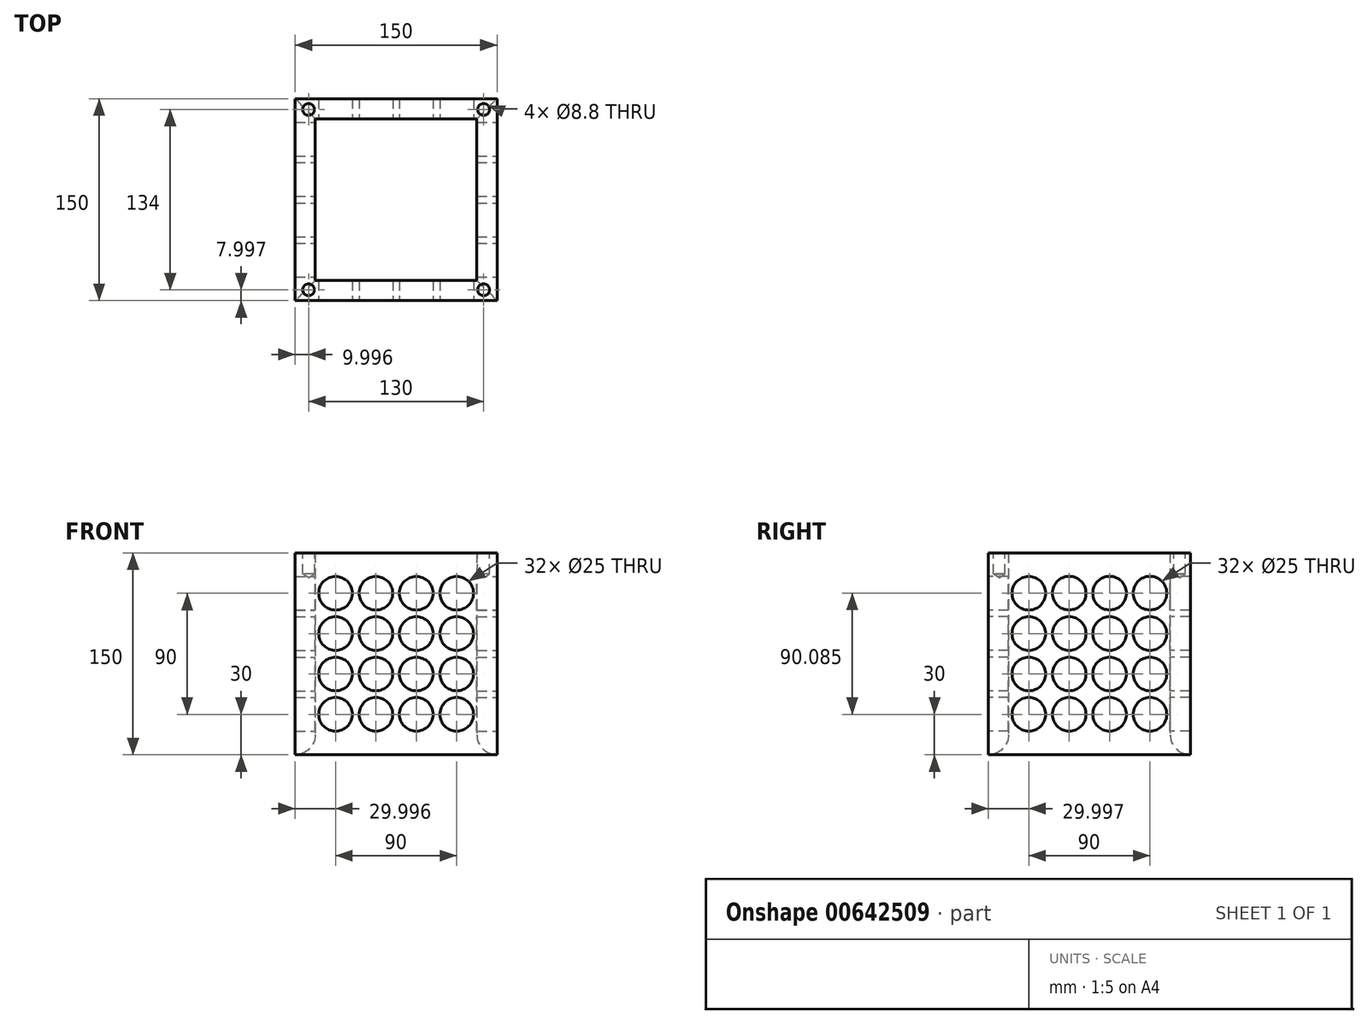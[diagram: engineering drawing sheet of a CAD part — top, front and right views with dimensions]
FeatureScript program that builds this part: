
annotation { "Feature Type Name" : "Feature", "Feature Type Description" : "" }
export const myFeature = defineFeature(function(context is Context, id is Id, definition is map)
    precondition{}
    {
        {
            var Q0;
            Q0=qCreatedBy(makeId("Top.planeOp"),FACE);
            var sketch = newSketch(context, id + "F0", { "sketchPlane" : qUnion([Q0])});
            skLineSegment(sketch, "E0.bottom", {"start": v(-58.65, 45.53) * mm, "end": v(-208.65, 45.53) * mm});
            skLineSegment(sketch, "E0.top", {"start": v(-58.65, -104.47) * mm, "end": v(-208.65, -104.47) * mm});
            skLineSegment(sketch, "E0.left", {"start": v(-58.65, 45.53) * mm, "end": v(-58.65, -104.47) * mm});
            skLineSegment(sketch, "E0.right", {"start": v(-208.65, 45.53) * mm, "end": v(-208.65, -104.47) * mm});
            skSolve(sketch);
        }
        {
            var Q0;
            Q0=makeQuery(id+"F0.imprint","IMPRINT",FACE,{"disambiguationData":[TD([[makeQuery(id+"F0.imprint","IMPRINT",EDGE,{"derivedFrom":sQuery(id+"F0.wireOp",EDGE,"E0.bottom")}),1.0]])]});
            extrude(context, id + "F1", {"entities" : qUnion([Q0]), "depth" : 150 * mm, "offsetDistance" : 25 * mm});
        }
        {
            var Q0;
            Q0=makeQuery(id+"F1.opExtrude","CAP_FACE",FACE,{"disambiguationData":[OSD([sQuery(id+"F0.wireOp",EDGE,"E0.bottom"),sQuery(id+"F0.wireOp",EDGE,"E0.top"),sQuery(id+"F0.wireOp",EDGE,"E0.left"),sQuery(id+"F0.wireOp",EDGE,"E0.right")])],"isStart":true});
            var Q1;
            Q1=makeQuery(id+"F1.opExtrude","CAP_FACE",FACE,{"disambiguationData":[OSD([sQuery(id+"F0.wireOp",EDGE,"E0.bottom"),sQuery(id+"F0.wireOp",EDGE,"E0.top"),sQuery(id+"F0.wireOp",EDGE,"E0.left"),sQuery(id+"F0.wireOp",EDGE,"E0.right")])],"isStart":false});
            shell(context, id + "F2", {"entities" : qUnion([Q0, Q1]), "thickness" : 15 * mm});
        }
        {
            var Q0;
            Q0=makeQuery(id+"F1.opExtrude","SWEPT_FACE",FACE,{"disambiguationData":[OSD([sQuery(id+"F0.wireOp",EDGE,"E0.top")])]});
            var sketch = newSketch(context, id + "F3", { "sketchPlane" : qUnion([Q0])});
            skPoint(sketch, "E1", {"position": v(-178.65, 120) * mm});
            skPoint(sketch, "E2", {"position": v(-178.65, 90) * mm});
            skPoint(sketch, "E3", {"position": v(-178.65, 60) * mm});
            skPoint(sketch, "E4", {"position": v(-178.65, 30) * mm});
            skPoint(sketch, "E5", {"position": v(-148.65, 120) * mm});
            skPoint(sketch, "E6", {"position": v(-118.65, 120) * mm});
            skPoint(sketch, "E7", {"position": v(-88.65, 120) * mm});
            skPoint(sketch, "E8", {"position": v(-148.65, 90) * mm});
            skPoint(sketch, "E9", {"position": v(-148.65, 60) * mm});
            skPoint(sketch, "E10", {"position": v(-148.65, 30) * mm});
            skPoint(sketch, "E11", {"position": v(-118.65, 90) * mm});
            skPoint(sketch, "E12", {"position": v(-118.65, 60) * mm});
            skPoint(sketch, "E13", {"position": v(-118.65, 30) * mm});
            skPoint(sketch, "E14", {"position": v(-88.65, 90) * mm});
            skPoint(sketch, "E15", {"position": v(-88.65, 60) * mm});
            skPoint(sketch, "E16", {"position": v(-88.65, 30) * mm});
            skSolve(sketch);
        }
        {
            var Q0;
            Q0=sQuery(id+"F3.wireOp",VERTEX,"E1");
            var Q1;
            Q1=sQuery(id+"F3.wireOp",VERTEX,"E5");
            var Q2;
            Q2=sQuery(id+"F3.wireOp",VERTEX,"E6");
            var Q3;
            Q3=sQuery(id+"F3.wireOp",VERTEX,"E7");
            var Q4;
            Q4=sQuery(id+"F3.wireOp",VERTEX,"E2");
            var Q5;
            Q5=sQuery(id+"F3.wireOp",VERTEX,"E8");
            var Q6;
            Q6=sQuery(id+"F3.wireOp",VERTEX,"E11");
            var Q7;
            Q7=sQuery(id+"F3.wireOp",VERTEX,"E14");
            var Q8;
            Q8=sQuery(id+"F3.wireOp",VERTEX,"E15");
            var Q9;
            Q9=sQuery(id+"F3.wireOp",VERTEX,"E12");
            var Q10;
            Q10=sQuery(id+"F3.wireOp",VERTEX,"E9");
            var Q11;
            Q11=sQuery(id+"F3.wireOp",VERTEX,"E3");
            var Q12;
            Q12=sQuery(id+"F3.wireOp",VERTEX,"E4");
            var Q13;
            Q13=sQuery(id+"F3.wireOp",VERTEX,"E10");
            var Q14;
            Q14=sQuery(id+"F3.wireOp",VERTEX,"E13");
            var Q15;
            Q15=sQuery(id+"F3.wireOp",VERTEX,"E16");
            var Q16;
            Q16=makeQuery(id+"F1.opExtrude","SWEPT_BODY",BODY,{"disambiguationData":[OSD([sQuery(id+"F0.wireOp",EDGE,"E0.bottom"),sQuery(id+"F0.wireOp",EDGE,"E0.top"),sQuery(id+"F0.wireOp",EDGE,"E0.left"),sQuery(id+"F0.wireOp",EDGE,"E0.right")])]});
            hole(context, id + "F4", {"style" : HoleStyle.SIMPLE, "endStyle" : HoleEndStyle.THROUGH, "holeDiameter" : 25 * mm, "majorDiameter" : 5 * mm, "isTappedThrough" : true, "tappedDepth" : 12 * mm, "tapClearance" : 3, "locations" : qUnion([Q0, Q1, Q2, Q3, Q4, Q5, Q6, Q7, Q8, Q9, Q10, Q11, Q12, Q13, Q14, Q15]), "scope" : qUnion([Q16])});
        }
        {
            var Q0;
            Q0=makeQuery(id+"F1.opExtrude","SWEPT_FACE",FACE,{"disambiguationData":[OSD([sQuery(id+"F0.wireOp",EDGE,"E0.left")])]});
            var sketch = newSketch(context, id + "F5", { "sketchPlane" : qUnion([Q0])});
            skPoint(sketch, "E17", {"position": v(-74.47, 205.73) * mm});
            skPoint(sketch, "E18", {"position": v(-38.58, 205.73) * mm});
            skPoint(sketch, "E19", {"position": v(8.94, 205.73) * mm});
            skPoint(sketch, "E20", {"position": v(0, 205.73) * mm});
            skPoint(sketch, "E21", {"position": v(-74.47, 176.17) * mm});
            skPoint(sketch, "E22", {"position": v(-74.47, 120) * mm});
            skPoint(sketch, "E23", {"position": v(-74.47, 90) * mm});
            skPoint(sketch, "E24", {"position": v(-74.47, 60) * mm});
            skPoint(sketch, "E25", {"position": v(-74.47, 30) * mm});
            skPoint(sketch, "E26", {"position": v(-44.47, 120.08) * mm});
            skPoint(sketch, "E27", {"position": v(-14.47, 120.08) * mm});
            skPoint(sketch, "E28", {"position": v(15.53, 120.08) * mm});
            skPoint(sketch, "E29", {"position": v(-44.47, 90) * mm});
            skPoint(sketch, "E30", {"position": v(-44.47, 60) * mm});
            skPoint(sketch, "E31", {"position": v(-44.47, 30) * mm});
            skPoint(sketch, "E32", {"position": v(-14.47, 90) * mm});
            skPoint(sketch, "E33", {"position": v(15.53, 90) * mm});
            skPoint(sketch, "E34", {"position": v(15.53, 60) * mm});
            skPoint(sketch, "E35", {"position": v(-14.47, 60) * mm});
            skPoint(sketch, "E36", {"position": v(-14.47, 30) * mm});
            skPoint(sketch, "E37", {"position": v(15.53, 30) * mm});
            skSolve(sketch);
        }
        {
            var Q0;
            Q0=sQuery(id+"F5.wireOp",VERTEX,"E22");
            var Q1;
            Q1=sQuery(id+"F5.wireOp",VERTEX,"E26");
            var Q2;
            Q2=sQuery(id+"F5.wireOp",VERTEX,"E27");
            var Q3;
            Q3=sQuery(id+"F5.wireOp",VERTEX,"E28");
            var Q4;
            Q4=sQuery(id+"F5.wireOp",VERTEX,"E23");
            var Q5;
            Q5=sQuery(id+"F5.wireOp",VERTEX,"E29");
            var Q6;
            Q6=sQuery(id+"F5.wireOp",VERTEX,"E32");
            var Q7;
            Q7=sQuery(id+"F5.wireOp",VERTEX,"E33");
            var Q8;
            Q8=sQuery(id+"F5.wireOp",VERTEX,"E34");
            var Q9;
            Q9=sQuery(id+"F5.wireOp",VERTEX,"E35");
            var Q10;
            Q10=sQuery(id+"F5.wireOp",VERTEX,"E30");
            var Q11;
            Q11=sQuery(id+"F5.wireOp",VERTEX,"E24");
            var Q12;
            Q12=sQuery(id+"F5.wireOp",VERTEX,"E25");
            var Q13;
            Q13=sQuery(id+"F5.wireOp",VERTEX,"E31");
            var Q14;
            Q14=sQuery(id+"F5.wireOp",VERTEX,"E36");
            var Q15;
            Q15=sQuery(id+"F5.wireOp",VERTEX,"E37");
            var Q16;
            Q16=makeQuery(id+"F1.opExtrude","SWEPT_BODY",BODY,{"disambiguationData":[OSD([sQuery(id+"F0.wireOp",EDGE,"E0.bottom"),sQuery(id+"F0.wireOp",EDGE,"E0.top"),sQuery(id+"F0.wireOp",EDGE,"E0.left"),sQuery(id+"F0.wireOp",EDGE,"E0.right")])]});
            hole(context, id + "F6", {"style" : HoleStyle.SIMPLE, "endStyle" : HoleEndStyle.THROUGH, "holeDiameter" : 25 * mm, "majorDiameter" : 5 * mm, "isTappedThrough" : true, "tappedDepth" : 12 * mm, "tapClearance" : 3, "locations" : qUnion([Q0, Q1, Q2, Q3, Q4, Q5, Q6, Q7, Q8, Q9, Q10, Q11, Q12, Q13, Q14, Q15]), "scope" : qUnion([Q16])});
        }
        {
            var Q0;
            {var subQ0=sQuery(id+"F0.wireOp",EDGE,"E0.top");Q0=makeQuery(id+"F2.opShell","OFFSET_EDGE",EDGE,{"disambiguationData":[OSD([subQ0]),TDD([makeQuery(id+"F1.opExtrude","CAP_EDGE",EDGE,{"disambiguationData":[OSD([subQ0])],"isStart":true})])]});}
            var Q1;
            {var subQ0=sQuery(id+"F0.wireOp",EDGE,"E0.left");Q1=makeQuery(id+"F2.opShell","OFFSET_EDGE",EDGE,{"disambiguationData":[OSD([subQ0]),TDD([makeQuery(id+"F1.opExtrude","CAP_EDGE",EDGE,{"disambiguationData":[OSD([subQ0])],"isStart":true})])]});}
            var Q2;
            {var subQ0=sQuery(id+"F0.wireOp",EDGE,"E0.bottom");Q2=makeQuery(id+"F2.opShell","OFFSET_EDGE",EDGE,{"disambiguationData":[OSD([subQ0]),TDD([makeQuery(id+"F1.opExtrude","CAP_EDGE",EDGE,{"disambiguationData":[OSD([subQ0])],"isStart":true})])]});}
            var Q3;
            {var subQ0=sQuery(id+"F0.wireOp",EDGE,"E0.right");Q3=makeQuery(id+"F2.opShell","OFFSET_EDGE",EDGE,{"disambiguationData":[OSD([subQ0]),TDD([makeQuery(id+"F1.opExtrude","CAP_EDGE",EDGE,{"disambiguationData":[OSD([subQ0])],"isStart":true})])]});}
            fillet(context, id + "F7", {"entities" : qUnion([Q0, Q1, Q2, Q3]), "radius" : 15 * mm, "tangentPropagation" : true, "allowEdgeOverflow" : false});
        }
        {
            var Q0;
            Q0=makeQuery(id+"F1.opExtrude","CAP_FACE",FACE,{"disambiguationData":[OSD([sQuery(id+"F0.wireOp",EDGE,"E0.bottom"),sQuery(id+"F0.wireOp",EDGE,"E0.top"),sQuery(id+"F0.wireOp",EDGE,"E0.left"),sQuery(id+"F0.wireOp",EDGE,"E0.right")])],"isStart":false});
            var sketch = newSketch(context, id + "F8", { "sketchPlane" : qUnion([Q0])});
            skPoint(sketch, "E38", {"position": v(-198.65, 37.53) * mm});
            skPoint(sketch, "E39", {"position": v(-68.65, -96.47) * mm});
            skPoint(sketch, "E40", {"position": v(-68.65, 37.53) * mm});
            skPoint(sketch, "E41", {"position": v(-198.65, -96.47) * mm});
            skSolve(sketch);
        }
        {
            var Q0;
            {var subQ6=sQuery(id+"F0.wireOp",EDGE,"E0.bottom");var subQ7=makeQuery(id+"F1.opExtrude","CAP_EDGE",EDGE,{"disambiguationData":[OSD([subQ6])],"isStart":false});Q0=makeQuery(id+"F8.imprint","IMPRINT",FACE,{"disambiguationData":[TD([[makeQuery(id+"F8.imprint","IMPRINT",EDGE,{"derivedFrom":subQ7}),1.0]])]});}
            var sketch = newSketch(context, id + "F9", { "sketchPlane" : qUnion([Q0])});
            skSolve(sketch);
        }
        {
            var Q0;
            Q0=sQuery(id+"F8.wireOp",VERTEX,"E38");
            var Q1;
            Q1=sQuery(id+"F8.wireOp",VERTEX,"E40");
            var Q2;
            Q2=sQuery(id+"F8.wireOp",VERTEX,"E39");
            var Q3;
            Q3=sQuery(id+"F8.wireOp",VERTEX,"E41");
            var Q4;
            Q4=makeQuery(id+"F1.opExtrude","SWEPT_BODY",BODY,{"disambiguationData":[OSD([sQuery(id+"F0.wireOp",EDGE,"E0.bottom"),sQuery(id+"F0.wireOp",EDGE,"E0.top"),sQuery(id+"F0.wireOp",EDGE,"E0.left"),sQuery(id+"F0.wireOp",EDGE,"E0.right")])]});
            hole(context, id + "F10", {"style" : HoleStyle.SIMPLE, "endStyle" : HoleEndStyle.BLIND, "standardTappedOrClearance" : lookupTablePath({ "standard" : "ISO", "engagement" : "75%", "pitch" : "1.25 mm", "size" : "M10", "type" : "Tapped" }), "standardBlindInLast" : lookupTablePath({ "standard" : "ISO", "engagement" : "75%", "pitch" : "1.25 mm", "size" : "M10", "type" : "Tapped" }), "holeDiameter" : 8.8 * mm, "majorDiameter" : 10 * mm, "showTappedDepth" : true, "holeDepth" : 15.75 * mm, "isTappedThrough" : true, "tappedDepth" : 12 * mm, "tapClearance" : 3, "locations" : qUnion([Q0, Q1, Q2, Q3]), "scope" : qUnion([Q4])});
        }
    });
